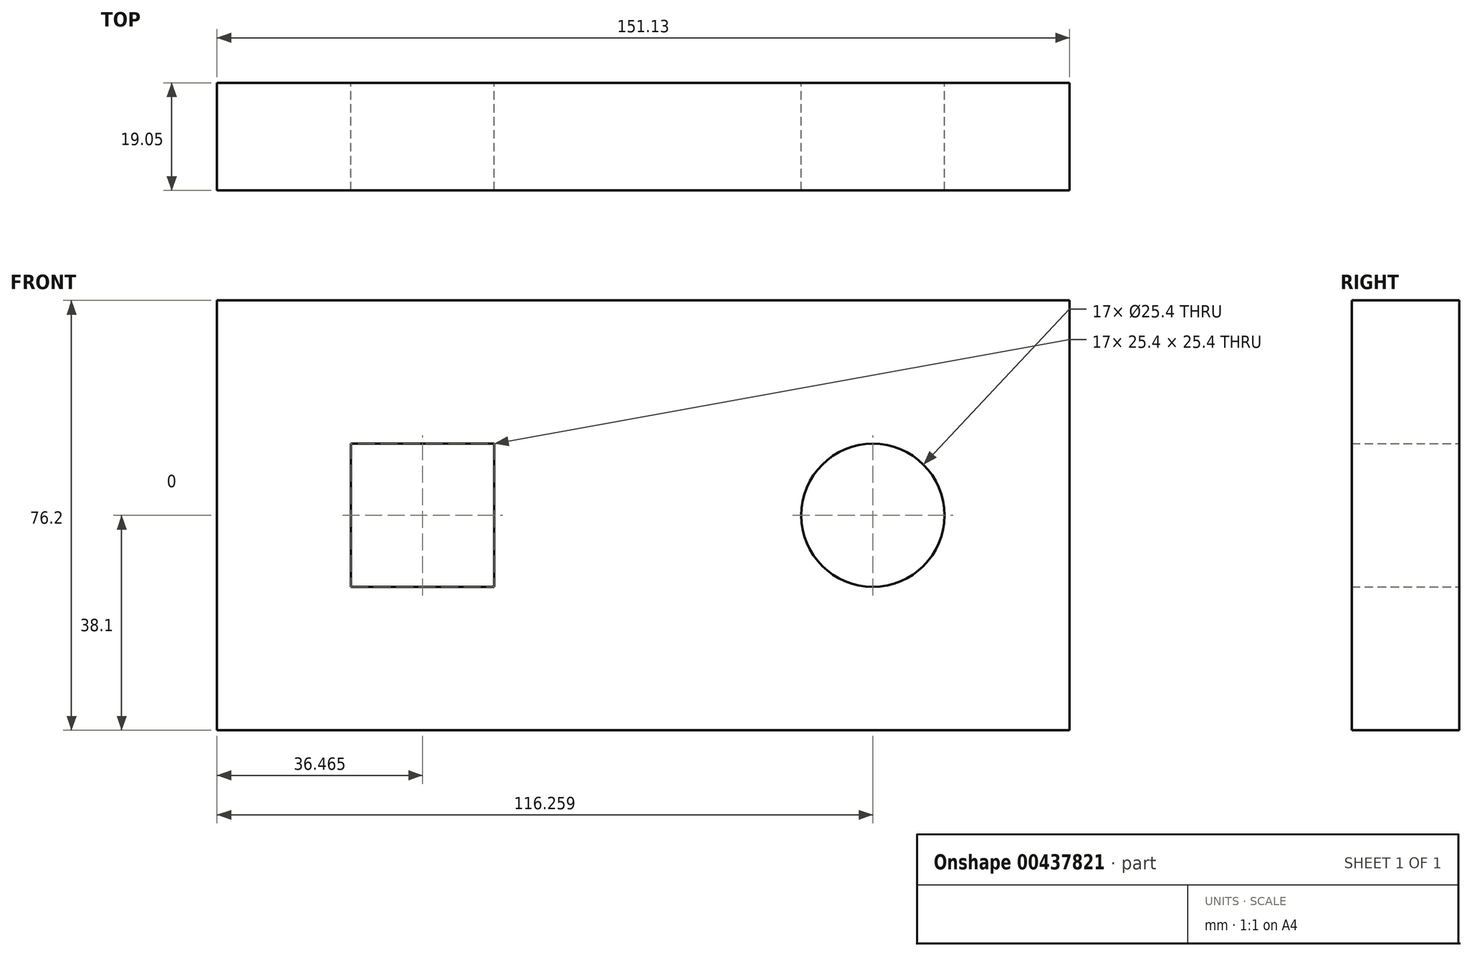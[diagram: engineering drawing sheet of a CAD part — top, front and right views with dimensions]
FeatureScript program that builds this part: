
annotation { "Feature Type Name" : "Feature", "Feature Type Description" : "" }
export const myFeature = defineFeature(function(context is Context, id is Id, definition is map)
    precondition{}
    {
        {
            var Q0;
            Q0=qCreatedBy(makeId("Front.planeOp"),FACE);
            var sketch = newSketch(context, id + "F0", { "sketchPlane" : qUnion([Q0])});
            skLineSegment(sketch, "E0.bottom", {"start": v(0, 0) * mm, "end": v(-151.13, 0) * mm});
            skLineSegment(sketch, "E0.top", {"start": v(0, 76.2) * mm, "end": v(-151.13, 76.2) * mm});
            skLineSegment(sketch, "E0.left", {"start": v(0, 0) * mm, "end": v(0, 76.2) * mm});
            skLineSegment(sketch, "E0.right", {"start": v(-151.13, 0) * mm, "end": v(-151.13, 76.2) * mm});
            skCircle(sketch, "E1", {"center": v(-34.87, 38.1) * mm, "radius": 12.7 * mm});
            skPoint(sketch, "E1.centerSnap0", {"position": v(0, 38.1) * mm});
            skLineSegment(sketch, "E2.bottom", {"start": v(-127.37, 50.8) * mm, "end": v(-101.97, 50.8) * mm});
            skLineSegment(sketch, "E2.top", {"start": v(-127.37, 25.4) * mm, "end": v(-101.97, 25.4) * mm});
            skLineSegment(sketch, "E2.left", {"start": v(-127.37, 50.8) * mm, "end": v(-127.37, 25.4) * mm});
            skLineSegment(sketch, "E2.right", {"start": v(-101.97, 50.8) * mm, "end": v(-101.97, 25.4) * mm});
            skPoint(sketch, "E2.middle", {"position": v(-114.67, 38.1) * mm});
            skPoint(sketch, "E2.middle.positionSnap0", {"position": v(-151.13, 38.1) * mm});
            skPoint(sketch, "E2.centerSnap0", {"position": v(-151.13, 38.1) * mm});
            skSolve(sketch);
        }
        {
            var Q0;
            Q0 = qSketchRegion(id + "F0", true);
            extrude(context, id + "F1", {"entities" : qUnion([Q0]), "depth" : 19.05 * mm});
        }
    });
